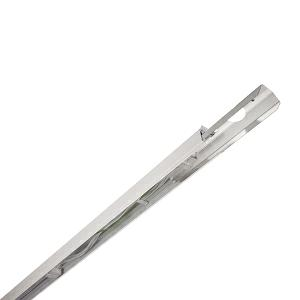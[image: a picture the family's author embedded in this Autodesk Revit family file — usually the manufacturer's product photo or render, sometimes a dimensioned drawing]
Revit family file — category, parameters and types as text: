
# Revit family: 3f_filippi_-_3f_linux_s_ip40_3f_filippi_-_a20017_-_3f_linux_s_5p_l3556
name_source: partatom
category: Lighting Fixtures
units: mm (PartAtom-declared; Revit-internal decimal feet)

## family parameters
Cut with Voids When Loaded = No
Host = Face
Light Source = No
Part Type = Normal
Room Calculation Point = No
Round Connector Dimension = Use Diameter
Shared = No

## types (1)
- 3F Filippi - 3F Linux S IP40
    Apparent Load = 0 VA
    Default Elevation = 1800 mm
    Description = Wired supporting structure for continuous channels, suitable for: lighting units 3F Linux L, 3F Linux D, 3F Linux DR, other luminaires or transport of electrical lines.

MECHANICAL
Wired base in hot galvanised steel and painted with polyester base in white colour, obtained through rolling process.
Saline-mist resistance equal to 500hrs and damp resistance equal to 700hrs.
Linear connecting element in hot galvanised steel already mounted on one end to form continuous channels.
Dimensions: 3556x62 mm, height 38 mm. Weight 3.94 kg.
IP40 protection degree.
Glow-wire test resistance 850°C.

ELECTRICAL
Through-wiring 5-poles with cables H07Z-U Halogen Free section 2.5 mm² HT90, with quick connecting terminal, irreversible, start / end and 2 intermediate power towers.

INSTALLATION
Ceiling / Suspended / Wall.
All accessories dedicated to this product are available on the Catalog and on our website www.3F-Filippi.com.

APPLICATIONS
Environments: commercial, exhibition areas, transit areas, lobbies or waiting rooms, shops, schools.

WARNING
Luminaire designed for disposal/recycling at end-of-life.
    Height = 38 mm
    Lamp = 0 x
    Length = 3556 mm
    Luminous efficacy = 0 lm/W
    Manufacturer = 3F Filippi
    ModVariant = No
    Model = 3F Filippi - A20017 - 3F Linux S 5P L3556
    Mounting Place = Ceiling
    Mounting Type = Pendant
    Number of Poles = 1
    OnlyDefault = Yes
    Power Factor = 1
    Product Name = 3F Filippi - 3F Linux S IP40
    Product group = Accessories
    ProductGroupID = 98
    Protection Class = Protection class
    Protection Degree = IP 40
    RLX_Detail_Level = 1
    RLX_Emergency_Light_Flux = 0 lm
    RLX_Emergency_Type = 0
    RLX_Emergency_Type_DB = No
    RlxData = <blob elided: 37497 chars, md5=e891f9c2>
    Standby Power = 0 W
    System Light Flux = 0 lm
    System Power = 0 W
    Type Comments = Product without accessories
    Type Image = 3ffilippi_3f_linux_s_ip40_l3556.jpg
    URL = http://relux.com
    VarID = ---
    Voltage = 0 V
    Weight = 0.00 kg
    Width = 62 mm  [stored 0.203412 ft]

note: [stored X ft] marks values corroborated as IEEE doubles in the binary element streams (Revit-internal decimal feet)

## geometry (parser evidence)
native form markers: Blend x4, Sweep x8
no freeform markers — native parametric forms only
